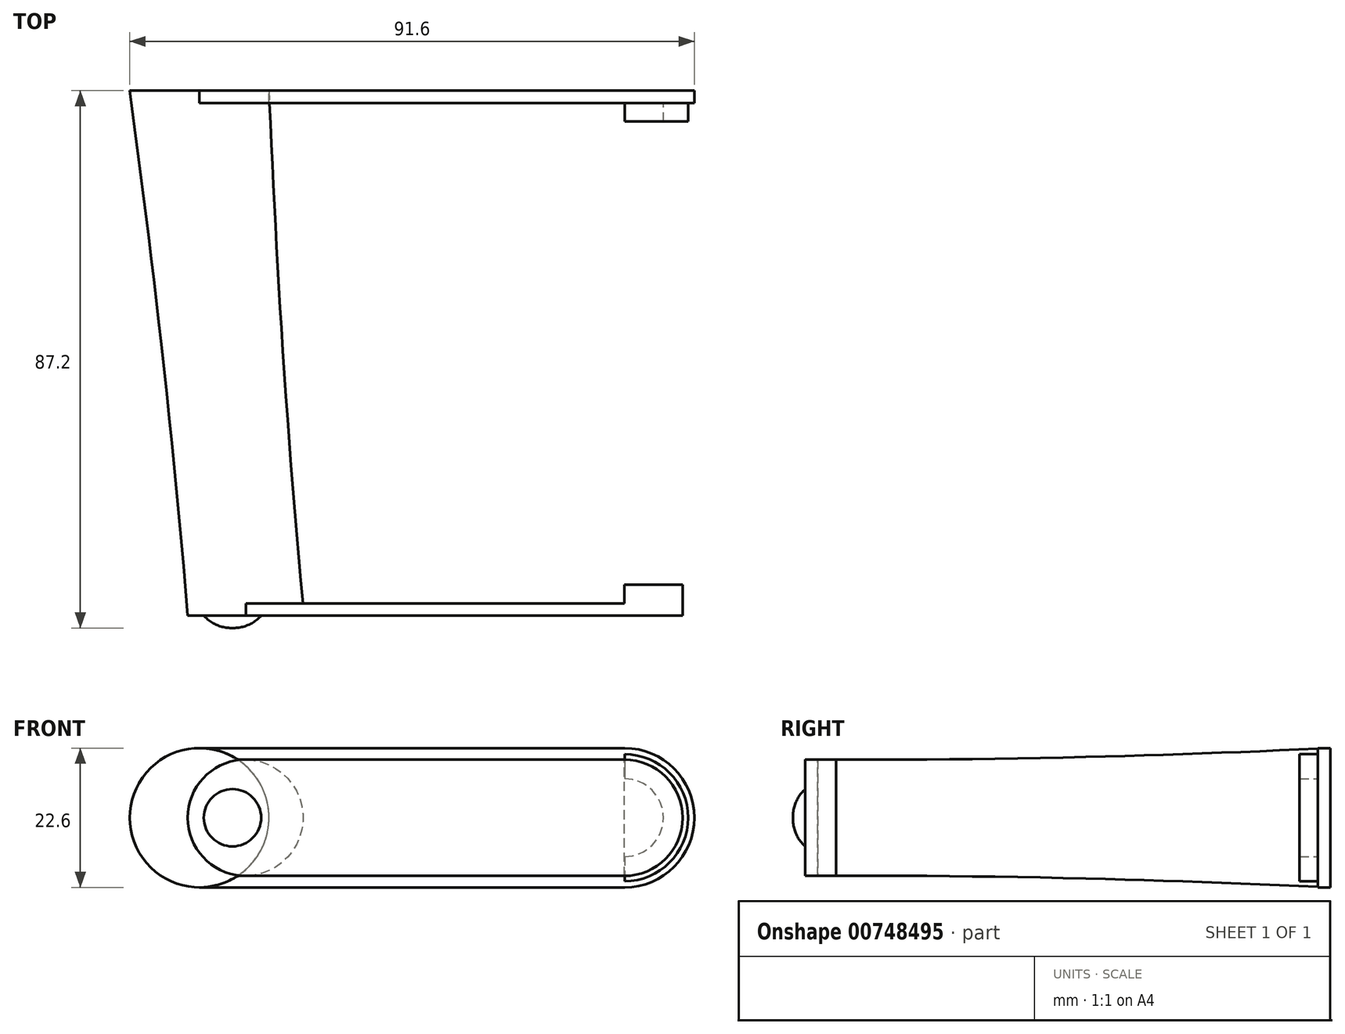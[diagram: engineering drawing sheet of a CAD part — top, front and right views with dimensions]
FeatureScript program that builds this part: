
annotation { "Feature Type Name" : "Feature", "Feature Type Description" : "" }
export const myFeature = defineFeature(function(context is Context, id is Id, definition is map)
    precondition{}
    {
        {
            var Q0;
            Q0=qCreatedBy(makeId("Front.planeOp"),FACE);
            var sketch = newSketch(context, id + "F0", { "sketchPlane" : qUnion([Q0])});
            skCircle(sketch, "E0", {"center": v(0, 0) * mm, "radius": 11.3 * mm});
            skLineSegment(sketch, "E1", {"start": v(0, 11.3) * mm, "end": v(69, 11.3) * mm});
            skLineSegment(sketch, "E2", {"start": v(0, -11.3) * mm, "end": v(69, -11.3) * mm});
            skLineSegment(sketch, "E3", {"start": v(69, 11.3) * mm, "end": v(69, 6.3) * mm});
            skLineSegment(sketch, "E4", {"start": v(69, -6.3) * mm, "end": v(69, -11.3) * mm});
            skArc(sketch, "E5", {"start": v(69, -11.3) * mm, "mid": v(80.3, 0) * mm, "end": v(69, 11.3) * mm});
            skArc(sketch, "E6", {"start": v(69, -6.3) * mm, "mid": v(75.3, 0) * mm, "end": v(69, 6.3) * mm});
            skArc(sketch, "E7", {"start": v(69, 10.3) * mm, "mid": v(79.3, 0) * mm, "end": v(69, -10.3) * mm});
            skArc(sketch, "E8", {"start": v(69, 7.3) * mm, "mid": v(76.3, 0) * mm, "end": v(69, -7.3) * mm});
            skSolve(sketch);
        }
        {
            var Q0;
            Q0=qCreatedBy(makeId("Front.planeOp"),FACE);
            cPlane(context, id + "F1", {"entities" : qUnion([Q0]), "cplaneType" : CPlaneType.OFFSET, "offset" : 85.2 * mm, "width" : 150 * mm, "height" : 150 * mm});
        }
        {
            var Q0;
            Q0=qCreatedBy(id+"F1.planeOp",FACE);
            var sketch = newSketch(context, id + "F2", { "sketchPlane" : qUnion([Q0])});
            skCircle(sketch, "E9", {"center": v(7.55, 0) * mm, "radius": 9.45 * mm});
            skSolve(sketch);
        }
        {
            var Q0;
            Q0=makeQuery(id+"F2.imprint","IMPRINT",FACE,{"disambiguationData":[TD([[makeQuery(id+"F2.imprint","IMPRINT",EDGE,{"derivedFrom":sQuery(id+"F2.wireOp",EDGE,"E9")}),1.0]])]});
            var Q1;
            {var subQ0=sQuery(id+"F0.wireOp",EDGE,"E0");var subQ1=makeQuery(id+"F0.imprint","INTERSECT",VERTEX,{"derivedFrom":[subQ0,sQuery(id+"F0.wireOp",EDGE,"E1")]});Q1=makeQuery(id+"F0.imprint","IMPRINT",FACE,{"disambiguationData":[TD([[makeQuery(id+"F0.imprint","IMPRINT",EDGE,{"disambiguationData":[TD([[subQ1,-1.0]])],"derivedFrom":subQ0}),1.0]])]});}
            loft(context, id + "F3", {"sheetProfilesArray" : [{ "sheetProfileEntities" : qUnion([Q0]) }, { "sheetProfileEntities" : qUnion([Q1]) }]});
        }
        {
            var Q0;
            {var subQ1=sQuery(id+"F0.wireOp",EDGE,"E1");Q0=makeQuery(id+"F0.imprint","IMPRINT",FACE,{"disambiguationData":[TD([[makeQuery(id+"F0.imprint","IMPRINT",EDGE,{"derivedFrom":subQ1}),-1.0]])]});}
            extrude(context, id + "F4", {"entities" : qUnion([Q0]), "depth" : 2 * mm, "offsetDistance" : 25 * mm});
        }
        {
            var Q0;
            Q0=makeQuery(id+"F0.imprint","IMPRINT",FACE,{"disambiguationData":[TD([[makeQuery(id+"F0.imprint","IMPRINT",EDGE,{"derivedFrom":sQuery(id+"F0.wireOp",EDGE,"E3")}),1.0]])]});
            extrude(context, id + "F5", {"entities" : qUnion([Q0]), "operationType" : NewBodyOperationType.ADD, "depth" : 5 * mm, "offsetDistance" : 25 * mm});
        }
        {
            var Q0;
            Q0=qCreatedBy(id+"F1.planeOp",FACE);
            var sketch = newSketch(context, id + "F6", { "sketchPlane" : qUnion([Q0])});
            skLineSegment(sketch, "E10.bottom", {"start": v(7.55, -9.45) * mm, "end": v(68.95, -9.45) * mm});
            skLineSegment(sketch, "E10.top", {"start": v(7.55, 9.45) * mm, "end": v(68.95, 9.45) * mm});
            skLineSegment(sketch, "E10.left", {"start": v(7.55, -9.45) * mm, "end": v(7.55, 9.45) * mm});
            skLineSegment(sketch, "E10.right", {"start": v(68.95, -9.45) * mm, "end": v(68.95, 9.45) * mm});
            skArc(sketch, "E11", {"start": v(68.95, -9.45) * mm, "mid": v(78.4, 0) * mm, "end": v(68.95, 9.45) * mm});
            skLineSegment(sketch, "E12", {"start": v(68.95, -3.52) * mm, "end": v(68.95, -3.52) * mm});
            skSolve(sketch);
        }
        {
            var Q0;
            Q0=makeQuery(id+"F6.imprint","IMPRINT",FACE,{"disambiguationData":[TD([[makeQuery(id+"F6.imprint","IMPRINT",EDGE,{"derivedFrom":sQuery(id+"F6.wireOp",EDGE,"E10.bottom")}),1.0]])]});
            extrude(context, id + "F7", {"entities" : qUnion([Q0]), "operationType" : NewBodyOperationType.ADD, "oppositeDirection" : true, "depth" : 2 * mm, "offsetDistance" : 25 * mm});
        }
        {
            var Q0;
            Q0=makeQuery(id+"F6.imprint","IMPRINT",FACE,{"disambiguationData":[TD([[makeQuery(id+"F6.imprint","IMPRINT",EDGE,{"derivedFrom":sQuery(id+"F6.wireOp",EDGE,"E10.right")}),-1.0]])]});
            extrude(context, id + "F8", {"entities" : qUnion([Q0]), "operationType" : NewBodyOperationType.ADD, "oppositeDirection" : true, "depth" : 5 * mm, "offsetDistance" : 25 * mm});
        }
        {
            var Q0;
            Q0=qCreatedBy(id+"F1.planeOp",FACE);
            var sketch = newSketch(context, id + "F9", { "sketchPlane" : qUnion([Q0])});
            skCircle(sketch, "E13", {"center": v(5.37, 0) * mm, "radius": 4.65 * mm});
            skSolve(sketch);
        }
        {
            var Q0;
            Q0=qSketchRegion(id+"F9",true);
            extrude(context, id + "F10", {"entities" : qUnion([Q0]), "operationType" : NewBodyOperationType.ADD, "depth" : 2 * mm, "offsetDistance" : 25 * mm});
        }
        {
            var Q0;
            Q0=makeQuery(id+"F10.opExtrude","CAP_FACE",FACE,{"disambiguationData":[OSD([sQuery(id+"F9.wireOp",EDGE,"E13")])],"isStart":false});
            fillet(context, id + "F11", {"entities" : qUnion([Q0]), "radius" : 6 * mm, "tangentPropagation" : true, "allowEdgeOverflow" : false});
        }
        {
            var Q0;
            {var subQ0=sQuery(id+"F0.wireOp",EDGE,"E7");Q0=makeQuery(id+"F0.imprint","IMPRINT",FACE,{"disambiguationData":[TD([[makeQuery(id+"F0.imprint","IMPRINT",EDGE,{"derivedFrom":subQ0}),-1.0]])]});}
            var Q1;
            Q1=sQuery(id+"F0.wireOp",EDGE,"E8");
            var Q2;
            Q2=sQuery(id+"F0.wireOp",EDGE,"E7");
            var Q3;
            Q3=makeQuery(id+"F5.opExtrude","CAP_FACE",FACE,{"disambiguationData":[OSD([sQuery(id+"F0.wireOp",EDGE,"E3"),sQuery(id+"F0.wireOp",EDGE,"E4"),sQuery(id+"F0.wireOp",EDGE,"E5"),sQuery(id+"F0.wireOp",EDGE,"E6")])],"isStart":false});
            extrude(context, id + "F12", {"entities" : qUnion([Q0]), "operationType" : NewBodyOperationType.REMOVE, "surfaceOperationType" : NewSurfaceOperationType.ADD, "surfaceEntities" : qUnion([Q1, Q2]), "endBound" : BoundingType.UP_TO_NEXT, "depth" : 25 * mm, "endBoundEntityFace" : qUnion([Q3]), "hasOffset" : true, "offsetDistance" : 1 * mm, "offsetOppositeDirection" : true});
        }
        {
            var Q0;
            {var subQ0=sQuery(id+"F0.wireOp",EDGE,"E7");Q0=makeQuery(id+"F0.imprint","IMPRINT",FACE,{"disambiguationData":[TD([[makeQuery(id+"F0.imprint","IMPRINT",EDGE,{"derivedFrom":subQ0}),-1.0]])]});}
            var Q1;
            Q1=makeQuery(id+"F4.opExtrude","CAP_FACE",FACE,{"disambiguationData":[OSD([sQuery(id+"F0.wireOp",EDGE,"E0"),sQuery(id+"F0.wireOp",EDGE,"E1"),sQuery(id+"F0.wireOp",EDGE,"E2"),sQuery(id+"F0.wireOp",EDGE,"E3"),sQuery(id+"F0.wireOp",EDGE,"E4"),sQuery(id+"F0.wireOp",EDGE,"E6")])],"isStart":false});
            extrude(context, id + "F13", {"entities" : qUnion([Q0]), "operationType" : NewBodyOperationType.ADD, "endBound" : BoundingType.UP_TO_SURFACE, "depth" : 1 * mm, "endBoundEntityFace" : qUnion([Q1]), "offsetDistance" : 25 * mm});
        }
    });
